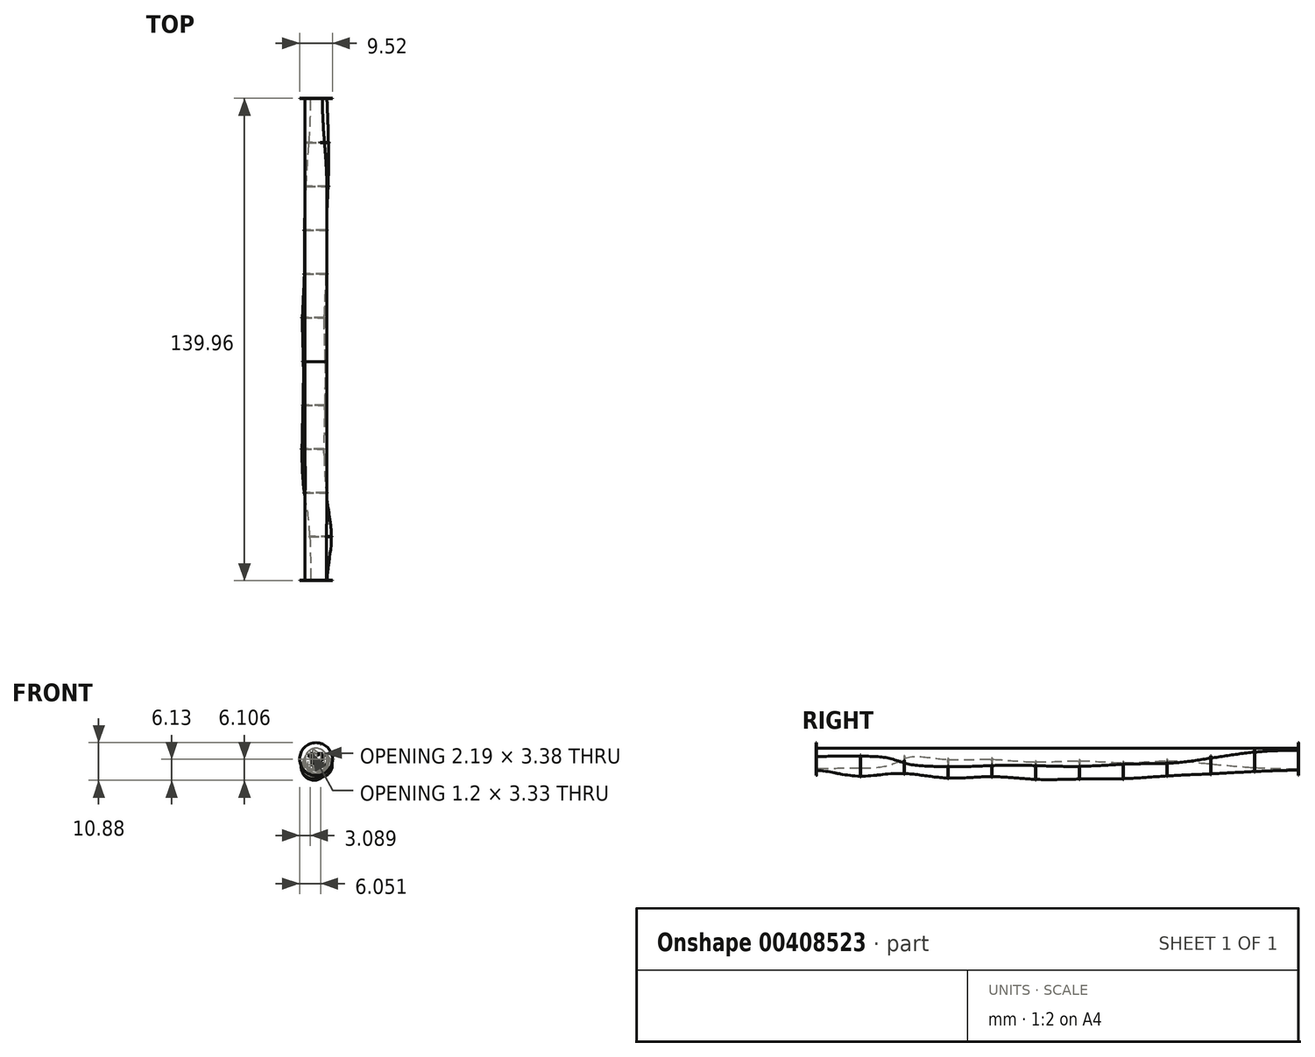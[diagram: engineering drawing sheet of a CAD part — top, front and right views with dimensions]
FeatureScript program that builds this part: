
annotation { "Feature Type Name" : "Feature", "Feature Type Description" : "" }
export const myFeature = defineFeature(function(context is Context, id is Id, definition is map)
    precondition{}
    {
        {
            var Q0;
            Q0=qCreatedBy(makeId("Front.planeOp"),FACE);
            var sketch = newSketch(context, id + "F0", { "sketchPlane" : qUnion([Q0])});
            skCircle(sketch, "E0", {"center": v(1.27, -1.78) * mm, "radius": 3.18 * mm});
            skSolve(sketch);
        }
        {
            var Q0;
            Q0=qCreatedBy(makeId("Right.planeOp"),FACE);
            var sketch = newSketch(context, id + "F1", { "sketchPlane" : qUnion([Q0])});
            skLineSegment(sketch, "E1", {"start": v(0, 0) * mm, "end": v(5953.12, 0) * mm});
            skSolve(sketch);
        }
        {
            var Q0;
            Q0=makeQuery(id+"F0.imprint","IMPRINT",FACE,{"disambiguationData":[TD([[makeQuery(id+"F0.imprint","IMPRINT",EDGE,{"derivedFrom":sQuery(id+"F0.wireOp",EDGE,"E0")}),1.0]])]});
            cPlane(context, id + "F2", {"entities" : qUnion([Q0]), "cplaneType" : CPlaneType.OFFSET, "offset" : 12.7 * mm, "oppositeDirection" : true, "width" : 152.4 * mm, "height" : 152.4 * mm});
        }
        {
            var Q0;
            Q0=qCreatedBy(id+"F2.planeOp",FACE);
            var sketch = newSketch(context, id + "F3", { "sketchPlane" : qUnion([Q0])});
            skCircle(sketch, "E2", {"center": v(-0.2, -1) * mm, "radius": 3.18 * mm});
            skSolve(sketch);
        }
        {
            var Q0;
            Q0=makeQuery(id+"F0.imprint","IMPRINT",FACE,{"disambiguationData":[TD([[makeQuery(id+"F0.imprint","IMPRINT",EDGE,{"derivedFrom":sQuery(id+"F0.wireOp",EDGE,"E0")}),1.0]])]});
            cPlane(context, id + "F4", {"entities" : qUnion([Q0]), "cplaneType" : CPlaneType.OFFSET, "offset" : 25.4 * mm, "oppositeDirection" : true, "width" : 152.4 * mm, "height" : 152.4 * mm});
        }
        {
            var Q0;
            Q0=makeQuery(id+"F0.imprint","IMPRINT",FACE,{"disambiguationData":[TD([[makeQuery(id+"F0.imprint","IMPRINT",EDGE,{"derivedFrom":sQuery(id+"F0.wireOp",EDGE,"E0")}),1.0]])]});
            cPlane(context, id + "F5", {"entities" : qUnion([Q0]), "cplaneType" : CPlaneType.OFFSET, "offset" : 38.1 * mm, "oppositeDirection" : true, "width" : 152.4 * mm, "height" : 152.4 * mm});
        }
        {
            var Q0;
            Q0=makeQuery(id+"F0.imprint","IMPRINT",FACE,{"disambiguationData":[TD([[makeQuery(id+"F0.imprint","IMPRINT",EDGE,{"derivedFrom":sQuery(id+"F0.wireOp",EDGE,"E0")}),1.0]])]});
            cPlane(context, id + "F6", {"entities" : qUnion([Q0]), "cplaneType" : CPlaneType.OFFSET, "offset" : 50.8 * mm, "oppositeDirection" : true, "width" : 152.4 * mm, "height" : 152.4 * mm});
        }
        {
            var Q0;
            Q0=makeQuery(id+"F0.imprint","IMPRINT",FACE,{"disambiguationData":[TD([[makeQuery(id+"F0.imprint","IMPRINT",EDGE,{"derivedFrom":sQuery(id+"F0.wireOp",EDGE,"E0")}),1.0]])]});
            cPlane(context, id + "F7", {"entities" : qUnion([Q0]), "cplaneType" : CPlaneType.OFFSET, "offset" : 63.5 * mm, "oppositeDirection" : true, "width" : 152.4 * mm, "height" : 152.4 * mm});
        }
        {
            var Q0;
            Q0=makeQuery(id+"F0.imprint","IMPRINT",FACE,{"disambiguationData":[TD([[makeQuery(id+"F0.imprint","IMPRINT",EDGE,{"derivedFrom":sQuery(id+"F0.wireOp",EDGE,"E0")}),1.0]])]});
            cPlane(context, id + "F8", {"entities" : qUnion([Q0]), "cplaneType" : CPlaneType.OFFSET, "offset" : 76.2 * mm, "oppositeDirection" : true, "width" : 152.4 * mm, "height" : 152.4 * mm});
        }
        {
            var Q0;
            Q0=makeQuery(id+"F0.imprint","IMPRINT",FACE,{"disambiguationData":[TD([[makeQuery(id+"F0.imprint","IMPRINT",EDGE,{"derivedFrom":sQuery(id+"F0.wireOp",EDGE,"E0")}),1.0]])]});
            cPlane(context, id + "F9", {"entities" : qUnion([Q0]), "cplaneType" : CPlaneType.OFFSET, "offset" : 88.9 * mm, "oppositeDirection" : true, "width" : 152.4 * mm, "height" : 152.4 * mm});
        }
        {
            var Q0;
            Q0=makeQuery(id+"F0.imprint","IMPRINT",FACE,{"disambiguationData":[TD([[makeQuery(id+"F0.imprint","IMPRINT",EDGE,{"derivedFrom":sQuery(id+"F0.wireOp",EDGE,"E0")}),1.0]])]});
            cPlane(context, id + "F10", {"entities" : qUnion([Q0]), "cplaneType" : CPlaneType.OFFSET, "offset" : 101.6 * mm, "oppositeDirection" : true, "width" : 152.4 * mm, "height" : 152.4 * mm});
        }
        {
            var Q0;
            Q0=makeQuery(id+"F0.imprint","IMPRINT",FACE,{"disambiguationData":[TD([[makeQuery(id+"F0.imprint","IMPRINT",EDGE,{"derivedFrom":sQuery(id+"F0.wireOp",EDGE,"E0")}),1.0]])]});
            cPlane(context, id + "F11", {"entities" : qUnion([Q0]), "cplaneType" : CPlaneType.OFFSET, "offset" : 114.3 * mm, "oppositeDirection" : true, "width" : 152.4 * mm, "height" : 152.4 * mm});
        }
        {
            var Q0;
            Q0=makeQuery(id+"F0.imprint","IMPRINT",FACE,{"disambiguationData":[TD([[makeQuery(id+"F0.imprint","IMPRINT",EDGE,{"derivedFrom":sQuery(id+"F0.wireOp",EDGE,"E0")}),1.0]])]});
            cPlane(context, id + "F12", {"entities" : qUnion([Q0]), "cplaneType" : CPlaneType.OFFSET, "offset" : 127 * mm, "oppositeDirection" : true, "width" : 152.4 * mm, "height" : 152.4 * mm});
        }
        {
            var Q0;
            Q0=makeQuery(id+"F0.imprint","IMPRINT",FACE,{"disambiguationData":[TD([[makeQuery(id+"F0.imprint","IMPRINT",EDGE,{"derivedFrom":sQuery(id+"F0.wireOp",EDGE,"E0")}),1.0]])]});
            cPlane(context, id + "F13", {"entities" : qUnion([Q0]), "cplaneType" : CPlaneType.OFFSET, "offset" : 12.7 * mm, "width" : 152.4 * mm, "height" : 152.4 * mm});
        }
        {
            var Q0;
            Q0=qCreatedBy(id+"F13.planeOp",FACE);
            var sketch = newSketch(context, id + "F14", { "sketchPlane" : qUnion([Q0])});
            skCircle(sketch, "E3", {"center": v(0, 0) * mm, "radius": 3.18 * mm});
            skSolve(sketch);
        }
        {
            var Q0;
            Q0=qCreatedBy(id+"F4.planeOp",FACE);
            var sketch = newSketch(context, id + "F15", { "sketchPlane" : qUnion([Q0])});
            skCircle(sketch, "E4", {"center": v(-0.89, -2.31) * mm, "radius": 3.18 * mm});
            skSolve(sketch);
        }
        {
            var Q0;
            Q0=qCreatedBy(id+"F5.planeOp",FACE);
            var sketch = newSketch(context, id + "F16", { "sketchPlane" : qUnion([Q0])});
            skCircle(sketch, "E5", {"center": v(-0.6, -1.9) * mm, "radius": 3.18 * mm});
            skSolve(sketch);
        }
        {
            var Q0;
            Q0=qCreatedBy(id+"F6.planeOp",FACE);
            var sketch = newSketch(context, id + "F17", { "sketchPlane" : qUnion([Q0])});
            skCircle(sketch, "E6", {"center": v(-0.5, -2.7) * mm, "radius": 3.18 * mm});
            skSolve(sketch);
        }
        {
            var Q0;
            Q0=qCreatedBy(id+"F7.planeOp",FACE);
            var sketch = newSketch(context, id + "F18", { "sketchPlane" : qUnion([Q0])});
            skCircle(sketch, "E7", {"center": v(-0.76, -2.6) * mm, "radius": 3.18 * mm});
            skSolve(sketch);
        }
        {
            var Q0;
            Q0=qCreatedBy(id+"F8.planeOp",FACE);
            var sketch = newSketch(context, id + "F19", { "sketchPlane" : qUnion([Q0])});
            skCircle(sketch, "E8", {"center": v(-0.2, -2.49) * mm, "radius": 3.18 * mm});
            skSolve(sketch);
        }
        {
            var Q0;
            Q0=qCreatedBy(id+"F9.planeOp",FACE);
            var sketch = newSketch(context, id + "F20", { "sketchPlane" : qUnion([Q0])});
            skCircle(sketch, "E9", {"center": v(-0.2, -1.7) * mm, "radius": 3.18 * mm});
            skSolve(sketch);
        }
        {
            var Q0;
            Q0=qCreatedBy(id+"F10.planeOp",FACE);
            var sketch = newSketch(context, id + "F21", { "sketchPlane" : qUnion([Q0])});
            skCircle(sketch, "E10", {"center": v(0.3, -1.1) * mm, "radius": 3.18 * mm});
            skSolve(sketch);
        }
        {
            var Q0;
            Q0=qCreatedBy(id+"F11.planeOp",FACE);
            var sketch = newSketch(context, id + "F22", { "sketchPlane" : qUnion([Q0])});
            skCircle(sketch, "E11", {"center": v(0.4, -0.4) * mm, "radius": 3.18 * mm});
            skSolve(sketch);
        }
        {
            var Q0;
            Q0=qCreatedBy(id+"F12.planeOp",FACE);
            var sketch = newSketch(context, id + "F23", { "sketchPlane" : qUnion([Q0])});
            skCircle(sketch, "E12", {"center": v(0, 0) * mm, "radius": 3.18 * mm});
            skSolve(sketch);
        }
        {
            var Q0;
            Q0=makeQuery(id+"F14.imprint","IMPRINT",FACE,{"disambiguationData":[TD([[makeQuery(id+"F14.imprint","IMPRINT",EDGE,{"derivedFrom":sQuery(id+"F14.wireOp",EDGE,"E3")}),1.0]])]});
            var Q1;
            Q1=makeQuery(id+"F0.imprint","IMPRINT",FACE,{"disambiguationData":[TD([[makeQuery(id+"F0.imprint","IMPRINT",EDGE,{"derivedFrom":sQuery(id+"F0.wireOp",EDGE,"E0")}),1.0]])]});
            var Q2;
            Q2=makeQuery(id+"F3.imprint","IMPRINT",FACE,{"disambiguationData":[TD([[makeQuery(id+"F3.imprint","IMPRINT",EDGE,{"derivedFrom":sQuery(id+"F3.wireOp",EDGE,"E2")}),1.0]])]});
            var Q3;
            Q3=makeQuery(id+"F15.imprint","IMPRINT",FACE,{"disambiguationData":[TD([[makeQuery(id+"F15.imprint","IMPRINT",EDGE,{"derivedFrom":sQuery(id+"F15.wireOp",EDGE,"E4")}),1.0]])]});
            var Q4;
            Q4=makeQuery(id+"F16.imprint","IMPRINT",FACE,{"disambiguationData":[TD([[makeQuery(id+"F16.imprint","IMPRINT",EDGE,{"derivedFrom":sQuery(id+"F16.wireOp",EDGE,"E5")}),1.0]])]});
            var Q5;
            Q5=makeQuery(id+"F17.imprint","IMPRINT",FACE,{"disambiguationData":[TD([[makeQuery(id+"F17.imprint","IMPRINT",EDGE,{"derivedFrom":sQuery(id+"F17.wireOp",EDGE,"E6")}),1.0]])]});
            var Q6;
            Q6=makeQuery(id+"F18.imprint","IMPRINT",FACE,{"disambiguationData":[TD([[makeQuery(id+"F18.imprint","IMPRINT",EDGE,{"derivedFrom":sQuery(id+"F18.wireOp",EDGE,"E7")}),1.0]])]});
            var Q7;
            Q7=makeQuery(id+"F19.imprint","IMPRINT",FACE,{"disambiguationData":[TD([[makeQuery(id+"F19.imprint","IMPRINT",EDGE,{"derivedFrom":sQuery(id+"F19.wireOp",EDGE,"E8")}),1.0]])]});
            var Q8;
            Q8=makeQuery(id+"F20.imprint","IMPRINT",FACE,{"disambiguationData":[TD([[makeQuery(id+"F20.imprint","IMPRINT",EDGE,{"derivedFrom":sQuery(id+"F20.wireOp",EDGE,"E9")}),1.0]])]});
            var Q9;
            Q9=makeQuery(id+"F21.imprint","IMPRINT",FACE,{"disambiguationData":[TD([[makeQuery(id+"F21.imprint","IMPRINT",EDGE,{"derivedFrom":sQuery(id+"F21.wireOp",EDGE,"E10")}),1.0]])]});
            var Q10;
            Q10=makeQuery(id+"F22.imprint","IMPRINT",FACE,{"disambiguationData":[TD([[makeQuery(id+"F22.imprint","IMPRINT",EDGE,{"derivedFrom":sQuery(id+"F22.wireOp",EDGE,"E11")}),1.0]])]});
            var Q11;
            Q11=makeQuery(id+"F23.imprint","IMPRINT",FACE,{"disambiguationData":[TD([[makeQuery(id+"F23.imprint","IMPRINT",EDGE,{"derivedFrom":sQuery(id+"F23.wireOp",EDGE,"E12")}),1.0]])]});
            var Q12;
            Q12=makeQuery(id+"F14.imprint","IMPRINT",FACE,{"disambiguationData":[TD([[makeQuery(id+"F14.imprint","IMPRINT",EDGE,{"derivedFrom":sQuery(id+"F14.wireOp",EDGE,"E3")}),1.0]])]});
            var Q13;
            Q13=makeQuery(id+"F0.imprint","IMPRINT",FACE,{"disambiguationData":[TD([[makeQuery(id+"F0.imprint","IMPRINT",EDGE,{"derivedFrom":sQuery(id+"F0.wireOp",EDGE,"E0")}),1.0]])]});
            var Q14;
            Q14=makeQuery(id+"F3.imprint","IMPRINT",FACE,{"disambiguationData":[TD([[makeQuery(id+"F3.imprint","IMPRINT",EDGE,{"derivedFrom":sQuery(id+"F3.wireOp",EDGE,"E2")}),1.0]])]});
            var Q15;
            Q15=makeQuery(id+"F15.imprint","IMPRINT",FACE,{"disambiguationData":[TD([[makeQuery(id+"F15.imprint","IMPRINT",EDGE,{"derivedFrom":sQuery(id+"F15.wireOp",EDGE,"E4")}),1.0]])]});
            var Q16;
            Q16=makeQuery(id+"F16.imprint","IMPRINT",FACE,{"disambiguationData":[TD([[makeQuery(id+"F16.imprint","IMPRINT",EDGE,{"derivedFrom":sQuery(id+"F16.wireOp",EDGE,"E5")}),1.0]])]});
            var Q17;
            Q17=makeQuery(id+"F17.imprint","IMPRINT",FACE,{"disambiguationData":[TD([[makeQuery(id+"F17.imprint","IMPRINT",EDGE,{"derivedFrom":sQuery(id+"F17.wireOp",EDGE,"E6")}),1.0]])]});
            var Q18;
            Q18=makeQuery(id+"F18.imprint","IMPRINT",FACE,{"disambiguationData":[TD([[makeQuery(id+"F18.imprint","IMPRINT",EDGE,{"derivedFrom":sQuery(id+"F18.wireOp",EDGE,"E7")}),1.0]])]});
            var Q19;
            Q19=makeQuery(id+"F19.imprint","IMPRINT",FACE,{"disambiguationData":[TD([[makeQuery(id+"F19.imprint","IMPRINT",EDGE,{"derivedFrom":sQuery(id+"F19.wireOp",EDGE,"E8")}),1.0]])]});
            var Q20;
            Q20=makeQuery(id+"F20.imprint","IMPRINT",FACE,{"disambiguationData":[TD([[makeQuery(id+"F20.imprint","IMPRINT",EDGE,{"derivedFrom":sQuery(id+"F20.wireOp",EDGE,"E9")}),1.0]])]});
            var Q21;
            Q21=makeQuery(id+"F21.imprint","IMPRINT",FACE,{"disambiguationData":[TD([[makeQuery(id+"F21.imprint","IMPRINT",EDGE,{"derivedFrom":sQuery(id+"F21.wireOp",EDGE,"E10")}),1.0]])]});
            var Q22;
            Q22=makeQuery(id+"F22.imprint","IMPRINT",FACE,{"disambiguationData":[TD([[makeQuery(id+"F22.imprint","IMPRINT",EDGE,{"derivedFrom":sQuery(id+"F22.wireOp",EDGE,"E11")}),1.0]])]});
            var Q23;
            Q23=makeQuery(id+"F23.imprint","IMPRINT",FACE,{"disambiguationData":[TD([[makeQuery(id+"F23.imprint","IMPRINT",EDGE,{"derivedFrom":sQuery(id+"F23.wireOp",EDGE,"E12")}),1.0]])]});
            loft(context, id + "F24", {"sheetProfilesArray" : [{ "sheetProfileEntities" : qUnion([Q0]) }, { "sheetProfileEntities" : qUnion([Q1]) }, { "sheetProfileEntities" : qUnion([Q2]) }, { "sheetProfileEntities" : qUnion([Q3]) }, { "sheetProfileEntities" : qUnion([Q4]) }, { "sheetProfileEntities" : qUnion([Q5]) }, { "sheetProfileEntities" : qUnion([Q6]) }, { "sheetProfileEntities" : qUnion([Q7]) }, { "sheetProfileEntities" : qUnion([Q8]) }, { "sheetProfileEntities" : qUnion([Q9]) }, { "sheetProfileEntities" : qUnion([Q10]) }, { "sheetProfileEntities" : qUnion([Q11]) }], "wireProfilesArray" : [{ "wireProfileEntities" : qUnion([Q12]) }, { "wireProfileEntities" : qUnion([Q13]) }, { "wireProfileEntities" : qUnion([Q14]) }, { "wireProfileEntities" : qUnion([Q15]) }, { "wireProfileEntities" : qUnion([Q16]) }, { "wireProfileEntities" : qUnion([Q17]) }, { "wireProfileEntities" : qUnion([Q18]) }, { "wireProfileEntities" : qUnion([Q19]) }, { "wireProfileEntities" : qUnion([Q20]) }, { "wireProfileEntities" : qUnion([Q21]) }, { "wireProfileEntities" : qUnion([Q22]) }, { "wireProfileEntities" : qUnion([Q23]) }]});
        }
        {
            var Q0;
            Q0=qCreatedBy(id+"F11.planeOp",FACE);
            var sketch = newSketch(context, id + "F25", { "sketchPlane" : qUnion([Q0])});
            skCircle(sketch, "E13", {"center": v(0.4, -0.4) * mm, "radius": 3.43 * mm});
            skSolve(sketch);
        }
        {
            var Q0;
            Q0 = qSketchRegion(id + "F25", true);
            extrude(context, id + "F26", {"entities" : qUnion([Q0]), "operationType" : NewBodyOperationType.ADD, "endBound" : BoundingType.SYMMETRIC, "depth" : 0.13 * mm});
        }
        {
            var Q0;
            Q0=makeQuery(id+"F24.opLoft","CAP_FACE",FACE,{"disambiguationData":[OSD([makeQuery(id+"F14.imprint","IMPRINT",FACE,{"disambiguationData":[TD([[makeQuery(id+"F14.imprint","IMPRINT",EDGE,{"derivedFrom":sQuery(id+"F14.wireOp",EDGE,"E3")}),1.0]])]})])],"isStart":true});
            var Q1;
            Q1=makeQuery(id+"F24.opLoft","CAP_FACE",FACE,{"disambiguationData":[OSD([makeQuery(id+"F23.imprint","IMPRINT",FACE,{"disambiguationData":[TD([[makeQuery(id+"F23.imprint","IMPRINT",EDGE,{"derivedFrom":sQuery(id+"F23.wireOp",EDGE,"E12")}),1.0]])]})])],"isStart":true});
            extrude(context, id + "F27", {"entities" : qUnion([Q0]), "oppositeDirection" : true, "endBoundEntityFace" : qUnion([Q1]), "depth" : 139.7 * mm});
        }
        {
            var Q0;
            Q0=qCreatedBy(id+"F11.planeOp",FACE);
            var sketch = newSketch(context, id + "F28", { "sketchPlane" : qUnion([Q0])});
            skCircle(sketch, "E14", {"center": v(0.4, -0.4) * mm, "radius": 3.43 * mm});
            skSolve(sketch);
        }
        {
            var Q0;
            Q0 = qSketchRegion(id + "F28", true);
            extrude(context, id + "F29", {"entities" : qUnion([Q0]), "endBound" : BoundingType.SYMMETRIC, "depth" : 0.13 * mm});
        }
        {
            var Q0;
            Q0=qCreatedBy(id+"F11.planeOp",FACE);
            var sketch = newSketch(context, id + "F30", { "sketchPlane" : qUnion([Q0])});
            skCircle(sketch, "E15", {"center": v(0.4, -0.4) * mm, "radius": 3.43 * mm});
            skSolve(sketch);
        }
        {
            var Q0;
            Q0 = qSketchRegion(id + "F30", true);
            extrude(context, id + "F31", {"entities" : qUnion([Q0]), "endBound" : BoundingType.SYMMETRIC, "depth" : 0.13 * mm});
        }
        {
            var Q0;
            Q0=qCreatedBy(id+"F10.planeOp",FACE);
            var sketch = newSketch(context, id + "F32", { "sketchPlane" : qUnion([Q0])});
            skCircle(sketch, "E16", {"center": v(0.3, -1.1) * mm, "radius": 3.43 * mm});
            skSolve(sketch);
        }
        {
            var Q0;
            Q0 = qSketchRegion(id + "F32", true);
            extrude(context, id + "F33", {"entities" : qUnion([Q0]), "operationType" : NewBodyOperationType.ADD, "endBound" : BoundingType.SYMMETRIC, "depth" : 0.13 * mm});
        }
        {
            var Q0;
            Q0=qCreatedBy(id+"F9.planeOp",FACE);
            var sketch = newSketch(context, id + "F34", { "sketchPlane" : qUnion([Q0])});
            skCircle(sketch, "E17", {"center": v(-0.2, -1.7) * mm, "radius": 3.43 * mm});
            skSolve(sketch);
        }
        {
            var Q0;
            Q0 = qSketchRegion(id + "F34", true);
            extrude(context, id + "F35", {"entities" : qUnion([Q0]), "operationType" : NewBodyOperationType.ADD, "endBound" : BoundingType.SYMMETRIC, "depth" : 0.13 * mm});
        }
        {
            var Q0;
            Q0=qCreatedBy(id+"F8.planeOp",FACE);
            var sketch = newSketch(context, id + "F36", { "sketchPlane" : qUnion([Q0])});
            skCircle(sketch, "E18", {"center": v(-0.2, -2.49) * mm, "radius": 3.43 * mm});
            skSolve(sketch);
        }
        {
            var Q0;
            Q0 = qSketchRegion(id + "F36", true);
            extrude(context, id + "F37", {"entities" : qUnion([Q0]), "operationType" : NewBodyOperationType.ADD, "endBound" : BoundingType.SYMMETRIC, "depth" : 0.13 * mm});
        }
        {
            var Q0;
            Q0=qCreatedBy(id+"F7.planeOp",FACE);
            var sketch = newSketch(context, id + "F38", { "sketchPlane" : qUnion([Q0])});
            skCircle(sketch, "E19", {"center": v(-0.76, -2.6) * mm, "radius": 3.43 * mm});
            skSolve(sketch);
        }
        {
            var Q0;
            Q0 = qSketchRegion(id + "F38", true);
            extrude(context, id + "F39", {"entities" : qUnion([Q0]), "operationType" : NewBodyOperationType.ADD, "endBound" : BoundingType.SYMMETRIC, "depth" : 0.13 * mm});
        }
        {
            var Q0;
            Q0=qCreatedBy(id+"F6.planeOp",FACE);
            var sketch = newSketch(context, id + "F40", { "sketchPlane" : qUnion([Q0])});
            skCircle(sketch, "E20", {"center": v(-0.5, -2.7) * mm, "radius": 3.43 * mm});
            skSolve(sketch);
        }
        {
            var Q0;
            Q0 = qSketchRegion(id + "F40", true);
            extrude(context, id + "F41", {"entities" : qUnion([Q0]), "operationType" : NewBodyOperationType.ADD, "endBound" : BoundingType.SYMMETRIC, "depth" : 0.13 * mm});
        }
        {
            var Q0;
            Q0=qCreatedBy(id+"F5.planeOp",FACE);
            var sketch = newSketch(context, id + "F42", { "sketchPlane" : qUnion([Q0])});
            skCircle(sketch, "E21", {"center": v(-0.6, -1.9) * mm, "radius": 3.43 * mm});
            skSolve(sketch);
        }
        {
            var Q0;
            Q0 = qSketchRegion(id + "F42", true);
            extrude(context, id + "F43", {"entities" : qUnion([Q0]), "operationType" : NewBodyOperationType.ADD, "endBound" : BoundingType.SYMMETRIC, "depth" : 0.13 * mm});
        }
        {
            var Q0;
            Q0=qCreatedBy(id+"F4.planeOp",FACE);
            var sketch = newSketch(context, id + "F44", { "sketchPlane" : qUnion([Q0])});
            skCircle(sketch, "E22", {"center": v(-0.89, -2.31) * mm, "radius": 3.43 * mm});
            skSolve(sketch);
        }
        {
            var Q0;
            Q0 = qSketchRegion(id + "F44", true);
            extrude(context, id + "F45", {"entities" : qUnion([Q0]), "operationType" : NewBodyOperationType.ADD, "endBound" : BoundingType.SYMMETRIC, "depth" : 0.13 * mm});
        }
        {
            var Q0;
            Q0=qCreatedBy(id+"F2.planeOp",FACE);
            var sketch = newSketch(context, id + "F46", { "sketchPlane" : qUnion([Q0])});
            skCircle(sketch, "E23", {"center": v(-0.2, -1) * mm, "radius": 3.43 * mm});
            skSolve(sketch);
        }
        {
            var Q0;
            Q0 = qSketchRegion(id + "F46", true);
            extrude(context, id + "F47", {"entities" : qUnion([Q0]), "operationType" : NewBodyOperationType.ADD, "endBound" : BoundingType.SYMMETRIC, "depth" : 0.13 * mm});
        }
        {
            var Q0;
            Q0=qCreatedBy(makeId("Front.planeOp"),FACE);
            var sketch = newSketch(context, id + "F48", { "sketchPlane" : qUnion([Q0])});
            skCircle(sketch, "E24", {"center": v(1.27, -1.78) * mm, "radius": 3.43 * mm});
            skSolve(sketch);
        }
        {
            var Q0;
            Q0 = qSketchRegion(id + "F48", true);
            extrude(context, id + "F49", {"entities" : qUnion([Q0]), "operationType" : NewBodyOperationType.ADD, "endBound" : BoundingType.SYMMETRIC, "depth" : 0.13 * mm});
        }
        {
            var Q0;
            Q0=makeQuery(id+"F24.opLoft","CAP_FACE",FACE,{"disambiguationData":[OSD([makeQuery(id+"F23.imprint","IMPRINT",FACE,{"disambiguationData":[TD([[makeQuery(id+"F23.imprint","IMPRINT",EDGE,{"derivedFrom":sQuery(id+"F23.wireOp",EDGE,"E12")}),1.0]])]})])],"isStart":true});
            var sketch = newSketch(context, id + "F50", { "sketchPlane" : qUnion([Q0])});
            skCircle(sketch, "E25", {"center": v(0, 0) * mm, "radius": 4.76 * mm});
            skCircle(sketch, "E26", {"center": v(0, 0) * mm, "radius": 3.18 * mm});
            skText(sketch, "E27", { "text": "1", "fontName": "OpenSans-Regular.ttf"});
            const initialGuessF50  = {"E27": [-0.00158, -0.00275, 1, 0, 0.0055]};
            skSetInitialGuess(sketch, initialGuessF50);
            skSolve(sketch);
        }
        {
            var Q0;
            Q0 = qSketchRegion(id + "F50", true);
            var Q1;
            Q1=makeQuery(id+"F50.imprint","IMPRINT",FACE,{"disambiguationData":[TD([[makeQuery(id+"F50.imprint","IMPRINT",EDGE,{"derivedFrom":sQuery(id+"F50.wireOp",EDGE,"E26")}),1.0]])]});
            extrude(context, id + "F51", {"entities" : qUnion([Q0, Q1]), "operationType" : NewBodyOperationType.ADD, "depth" : 0.13 * mm});
        }
        {
            var Q0;
            Q0=qCreatedBy(id+"F13.planeOp",FACE);
            var sketch = newSketch(context, id + "F52", { "sketchPlane" : qUnion([Q0])});
            skCircle(sketch, "E28", {"center": v(0, 0) * mm, "radius": 4.76 * mm});
            skCircle(sketch, "E29", {"center": v(0, 0) * mm, "radius": 3.18 * mm});
            skText(sketch, "E30", { "text": "12", "fontName": "OpenSans-Regular.ttf"});
            const initialGuessF52  = {"E30": [-0.0027, -0.00168, 1, 0, 0.00336]};
            skSetInitialGuess(sketch, initialGuessF52);
            skSolve(sketch);
        }
        {
            var Q0;
            Q0 = qSketchRegion(id + "F52", true);
            var Q1;
            Q1=makeQuery(id+"F52.imprint","IMPRINT",FACE,{"disambiguationData":[TD([[makeQuery(id+"F52.imprint","IMPRINT",EDGE,{"derivedFrom":sQuery(id+"F52.wireOp",EDGE,"E29")}),1.0]])]});
            extrude(context, id + "F53", {"entities" : qUnion([Q0, Q1]), "depth" : 0.13 * mm});
        }
        {
            var Q0;
            Q0=qCreatedBy(id+"F11.planeOp",FACE);
            var sketch = newSketch(context, id + "F54", { "sketchPlane" : qUnion([Q0])});
            skCircle(sketch, "E31", {"center": v(0.4, -0.4) * mm, "radius": 3.43 * mm});
            skSolve(sketch);
        }
        {
            var Q0;
            Q0=makeQuery(id+"F54.imprint","IMPRINT",FACE,{"disambiguationData":[TD([[makeQuery(id+"F54.imprint","IMPRINT",EDGE,{"derivedFrom":sQuery(id+"F54.wireOp",EDGE,"E31")}),1.0]])]});
            extrude(context, id + "F55", {"entities" : qUnion([Q0]), "endBound" : BoundingType.SYMMETRIC, "depth" : 0.13 * mm});
        }
        {
            var Q0;
            Q0=makeQuery(id+"F55.opExtrude","SWEPT_BODY",BODY,{"disambiguationData":[OSD([sQuery(id+"F54.wireOp",EDGE,"E31")])]});
            deleteBodies(context, id + "F56", {"entities" : qUnion([Q0])});
        }
        {
            var Q0;
            Q0=makeQuery(id+"F31.opExtrude","SWEPT_BODY",BODY,{"disambiguationData":[OSD([sQuery(id+"F30.wireOp",EDGE,"E15")])]});
            deleteBodies(context, id + "F57", {"entities" : qUnion([Q0])});
        }
        {
            var Q0;
            Q0=makeQuery(id+"F29.opExtrude","SWEPT_BODY",BODY,{"disambiguationData":[OSD([sQuery(id+"F28.wireOp",EDGE,"E14")])]});
            deleteBodies(context, id + "F58", {"entities" : qUnion([Q0])});
        }
    });
